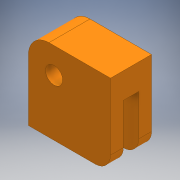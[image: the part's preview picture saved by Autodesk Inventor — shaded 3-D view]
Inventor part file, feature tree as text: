
AUTODESK INVENTOR PART (.ipt)
format: ipt  version: 2017 (Build 210142000, 142)  size: 166,400 bytes
history: native  units: mm
features: sketch x5, extrude x4, fillet x2, plane x1, projected_geometry x1
ambient origin geometry x8: Origin, YZ Plane, XZ Plane, XY Plane, X Axis, Y Axis, Z Axis, Center Point
bodies: Solid1 (feature_tree)
feature tree (13):
  extrude  "Extrusion1"  Depth=5.0mm
  extrude  "Extrusion2"  Depth=3.0mm
  plane  "Work Plane1"
  extrude  "Extrusion3"  Depth=8.0mm TaperAngle=0.0deg
  sketch  "Sketch4"  dims[d7=2.5mm d8=0.0mm d9=3.0mm d10=2.5mm d11=0.0mm d21=3.333333mm]
  extrude  "Extrusion4"  Depth=3.0mm
  fillet  "Fillet2"  Radius=2.5mm
  fillet  "Fillet3"  Radius=3.333333mm
  sketch  "Sketch1"  dims[d0=5.0mm d1=5.0mm]
  sketch  "Sketch2"  dims[d2=8.0mm d3=3.0mm]
  sketch  "Sketch3"  dims[d4=8.0mm d5=8.0mm d6=0.0mm]
  projected_geometry  "Projected Loop1"
  sketch  "Sketch5"  dims[d22=3.333333mm d23=3.333333mm d24=2.5mm d25=0.0mm d26=0.25mm d27=4.0mm]
